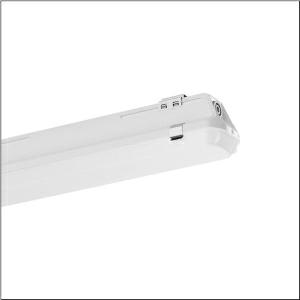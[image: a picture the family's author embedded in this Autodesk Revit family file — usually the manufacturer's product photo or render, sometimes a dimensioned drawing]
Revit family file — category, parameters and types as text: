
# Revit family: monsun_r__21_51fb10dp460b_c90e
name_source: partatom
category: Lighting Fixtures
units: mm (PartAtom-declared; Revit-internal decimal feet)

## family parameters
Cut with Voids When Loaded = No
Host = Face
Light Source = No
Part Type = Normal
Room Calculation Point = No
Round Connector Dimension = Use Diameter
Shared = No

## types (1)
- --- (1 x LED, 6060 lm, 39.4 W, 4000K)
    Apparent Load = 39 VA
    CIE Flux Codes = 47 77 93 94 100
    Color Rendering = 80
    Color Temperature = 4000K
    Default Elevation = 1800 mm
    Description = Monsun® 21, damp-proof luminaire, chain hanger, primary optical cover: enclosure, of PMMA, light emission: direct distribution, primary light characteristic: symmetric, installation type: suspended mounting, surface-mounted, horizontal mounting, vertical mounting, LED, rated luminous flux: 6.060lm, luminous efficacy: 154lm/W, light colour: 840, colour temperature: 4000K, control gear: ECG DALI, with terminal, 5-pole, max. 2.5mm², mains connection: 220..240V, AC, 50/60Hz, rated input power: 39W, housing, of glass-fibre reinforced polyester, uncoated, bright grey, incl. chain hanger, length: 1.590mm, width: 90mm, height: 88mm, clip for enclosure, of stainless steel (V2A), ceiling mounting element, of stainless steel (V2A), chain hanger, of stainless steel (V2A), protection rating (complete): IP66, insulation class (complete): insulation class I (protective earthing), certification: CE, ENEC, VDE, UKCA, protection symbol: D, impact resistance: IK04, permissible operating ambient temperature: -25..+35°C, standard: EN 50419, EN 60598-2-1, corresponds to IFS (International Featured Standards) requirements for safety and quality in the food industry, for indoor or canopied outdoor use, no direct snow, no direct sun, no direct rain, contact your sales advisor before using the luminaires in applications with unclear chemical exposure, large temperature fluctuations or condensation-forming humidity, LABS conformity tested according to VDMA 24364:2018-05, packaging unit: 1 piece
    Height = 89 mm
    Lamp = 1 x LED
    Lamp Light Flux = 6060 lm
    Lamp Power = 39.4 W
    Lamp count = 1
    Length = 1590 mm
    Luminous efficacy = 154 lm/W
    Manufacturer = Siteco
    ModVariant = No
    Model = 51FB10DP460B
    Mounting Place = Ceiling
    Mounting Type = Surface mounted
    Number of Poles = 1
    OnlyDefault = Yes
    Power Factor = 1
    Product Name = Monsun® 21
    Product group = damp-proof luminaire
    ProductGroupID = 300
    Protection Class = Protection class I
    Protection Degree = IP 66
    RLX_Detail_Level = 1
    RLX_Emergency_Light_Flux = 0 lm
    RLX_Emergency_Type = 0
    RLX_Emergency_Type_DB = No
    RlxData = <blob elided: 91845 chars, md5=87de7ad9>
    Socket = socket
    Standby Power = 0 W
    System Light Flux = 6060 lm
    System Power = 39 W
    Type Comments = factory setting: luminous flux: 100 % | dim-lin: 254 | 261 mA
    Type Image = l_1319656.jpg
    URL = http://relux.com
    VarID = @adj_171305
    Voltage = 0 V
    Weight = 0.00 kg
    Width = 90 mm

## geometry (parser evidence)
native form markers: Blend x4, Sweep x13
no freeform markers — native parametric forms only
